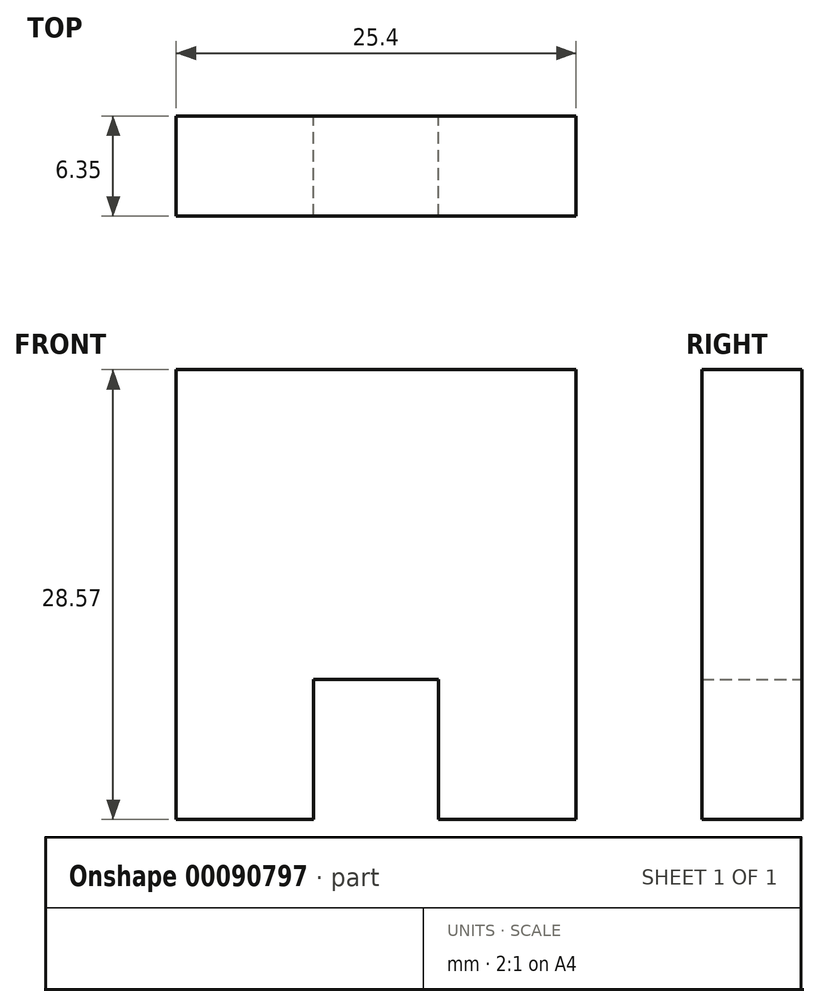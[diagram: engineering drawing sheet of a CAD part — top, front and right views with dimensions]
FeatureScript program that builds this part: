
annotation { "Feature Type Name" : "Feature", "Feature Type Description" : "" }
export const myFeature = defineFeature(function(context is Context, id is Id, definition is map)
    precondition{}
    {
        {
            var Q0;
            Q0=qCreatedBy(makeId("Front.planeOp"),FACE);
            var sketch = newSketch(context, id + "F0", { "sketchPlane" : qUnion([Q0])});
            skLineSegment(sketch, "E0.bottom", {"start": v(0, 0) * mm, "end": v(25.4, 0) * mm});
            skLineSegment(sketch, "E0.top", {"start": v(0, -28.57) * mm, "end": v(25.4, -28.57) * mm});
            skLineSegment(sketch, "E0.left", {"start": v(0, 0) * mm, "end": v(0, -28.57) * mm});
            skLineSegment(sketch, "E0.right", {"start": v(25.4, 0) * mm, "end": v(25.4, -28.57) * mm});
            skLineSegment(sketch, "E1.bottom", {"start": v(12.7, -28.57) * mm, "end": v(8.73, -28.57) * mm});
            skLineSegment(sketch, "E1.top", {"start": v(12.7, -19.69) * mm, "end": v(8.73, -19.69) * mm});
            skLineSegment(sketch, "E1.left", {"start": v(12.7, -28.57) * mm, "end": v(12.7, -19.69) * mm});
            skLineSegment(sketch, "E1.right", {"start": v(8.73, -28.58) * mm, "end": v(8.73, -19.69) * mm});
            skLineSegment(sketch, "E2.MirrorCS", {"start": v(12.7, -19.69) * mm, "end": v(16.67, -19.69) * mm});
            skLineSegment(sketch, "E3.MirrorCS", {"start": v(16.67, -28.58) * mm, "end": v(16.67, -19.69) * mm});
            skLineSegment(sketch, "E4.MirrorCS", {"start": v(12.7, -28.57) * mm, "end": v(16.67, -28.57) * mm});
            skSolve(sketch);
        }
        {
            var Q0;
            Q0=makeQuery(id+"F0.imprint","IMPRINT",FACE,{"disambiguationData":[TD([[makeQuery(id+"F0.imprint","IMPRINT",EDGE,{"derivedFrom":sQuery(id+"F0.wireOp",EDGE,"E0.bottom")}),-1.0]])]});
            extrude(context, id + "F1", {"entities" : qUnion([Q0]), "depth" : 6.35 * mm});
        }
    });
